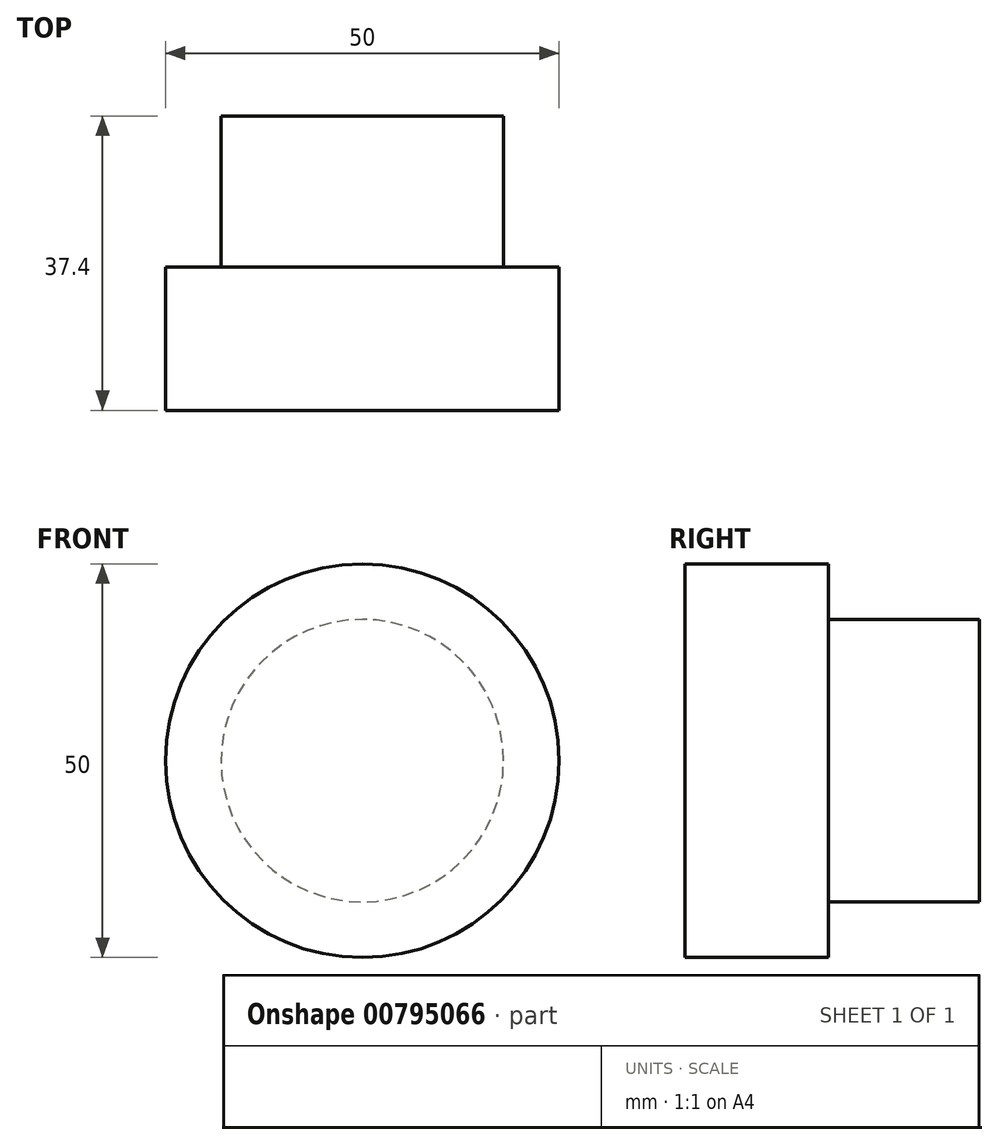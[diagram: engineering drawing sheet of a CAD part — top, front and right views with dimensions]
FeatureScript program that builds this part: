
annotation { "Feature Type Name" : "Feature", "Feature Type Description" : "" }
export const myFeature = defineFeature(function(context is Context, id is Id, definition is map)
    precondition{}
    {
        {
            var Q0;
            Q0=qCreatedBy(makeId("Front.planeOp"),FACE);
            var sketch = newSketch(context, id + "F0", { "sketchPlane" : qUnion([Q0])});
            skCircle(sketch, "E0", {"center": v(0, 0) * mm, "radius": 17.94 * mm});
            skSolve(sketch);
        }
        {
            var Q0;
            Q0 = qSketchRegion(id + "F0", true);
            extrude(context, id + "F1", {"entities" : qUnion([Q0]), "oppositeDirection" : true, "depth" : 19.2 * mm, "offsetDistance" : 25 * mm});
        }
        {
            var Q0;
            Q0=qCreatedBy(makeId("Front.planeOp"),FACE);
            var sketch = newSketch(context, id + "F2", { "sketchPlane" : qUnion([Q0])});
            skCircle(sketch, "E1", {"center": v(0, 0) * mm, "radius": 25 * mm});
            skSolve(sketch);
        }
        {
            var Q0;
            Q0 = qSketchRegion(id + "F2", true);
            extrude(context, id + "F3", {"entities" : qUnion([Q0]), "operationType" : NewBodyOperationType.ADD, "depth" : 18.2 * mm, "offsetDistance" : 25 * mm});
        }
    });
